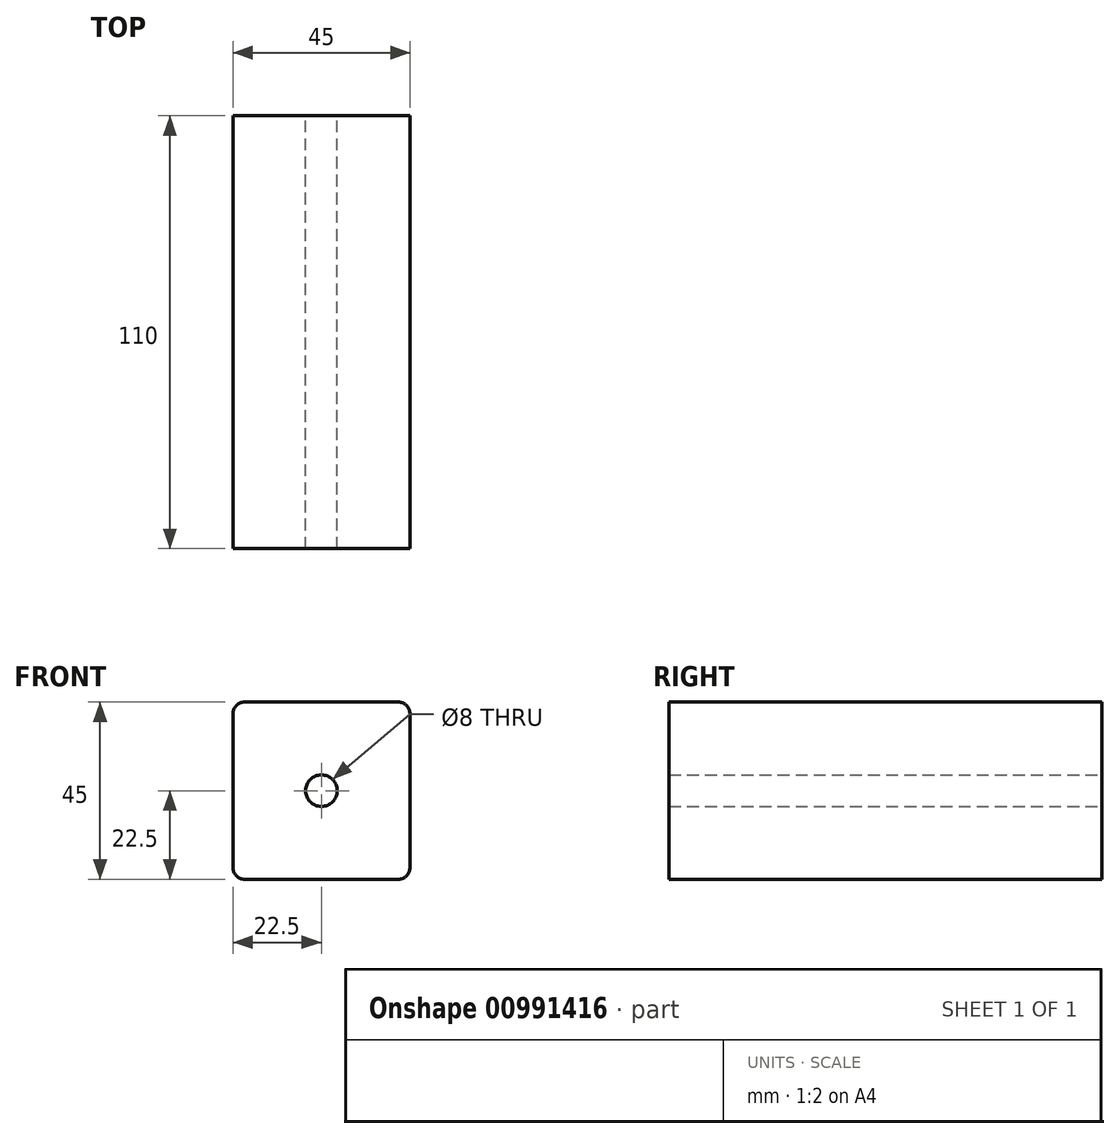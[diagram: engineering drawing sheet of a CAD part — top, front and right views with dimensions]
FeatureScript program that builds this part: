
annotation { "Feature Type Name" : "Feature", "Feature Type Description" : "" }
export const myFeature = defineFeature(function(context is Context, id is Id, definition is map)
    precondition{}
    {
        {
            var Q0;
            Q0=qCreatedBy(makeId("Front.planeOp"),FACE);
            var sketch = newSketch(context, id + "F0", { "sketchPlane" : qUnion([Q0])});
            skLineSegment(sketch, "E0.bottom", {"start": v(0, 0) * mm, "end": v(45, 0) * mm});
            skLineSegment(sketch, "E0.top", {"start": v(0, 45) * mm, "end": v(45, 45) * mm});
            skLineSegment(sketch, "E0.left", {"start": v(0, 0) * mm, "end": v(0, 45) * mm});
            skLineSegment(sketch, "E0.right", {"start": v(45, 0) * mm, "end": v(45, 45) * mm});
            skPoint(sketch, "E1", {"position": v(22.5, 22.5) * mm});
            skPoint(sketch, "E1.positionSnap0", {"position": v(45, 22.5) * mm});
            skPoint(sketch, "E1.positionSnap1", {"position": v(22.5, 45) * mm});
            skCircle(sketch, "E2", {"center": v(22.5, 22.5) * mm, "radius": 4 * mm});
            skSolve(sketch);
        }
        {
            var Q0;
            Q0=makeQuery(id+"F0.imprint","IMPRINT",FACE,{"disambiguationData":[TD([[makeQuery(id+"F0.imprint","IMPRINT",EDGE,{"derivedFrom":sQuery(id+"F0.wireOp",EDGE,"E0.bottom")}),1.0]])]});
            extrude(context, id + "F1", {"entities" : qUnion([Q0]), "depth" : 110 * mm, "offsetDistance" : 25 * mm});
        }
        {
            var Q0;
            Q0=makeQuery(id+"F1.opExtrude","SWEPT_EDGE",EDGE,{"disambiguationData":[OSD([sQuery(id+"F0.wireOp",EDGE,"E0.top"),sQuery(id+"F0.wireOp",EDGE,"E0.right")])]});
            var Q1;
            Q1=makeQuery(id+"F1.opExtrude","SWEPT_EDGE",EDGE,{"disambiguationData":[OSD([sQuery(id+"F0.wireOp",EDGE,"E0.bottom"),sQuery(id+"F0.wireOp",EDGE,"E0.right")])]});
            var Q2;
            Q2=makeQuery(id+"F1.opExtrude","SWEPT_EDGE",EDGE,{"disambiguationData":[OSD([sQuery(id+"F0.wireOp",EDGE,"E0.bottom"),sQuery(id+"F0.wireOp",EDGE,"E0.left")])]});
            var Q3;
            Q3=makeQuery(id+"F1.opExtrude","SWEPT_EDGE",EDGE,{"disambiguationData":[OSD([sQuery(id+"F0.wireOp",EDGE,"E0.top"),sQuery(id+"F0.wireOp",EDGE,"E0.left")])]});
            fillet(context, id + "F2", {"entities" : qUnion([Q0, Q1, Q2, Q3]), "radius" : 3 * mm, "tangentPropagation" : true, "allowEdgeOverflow" : false});
        }
    });
